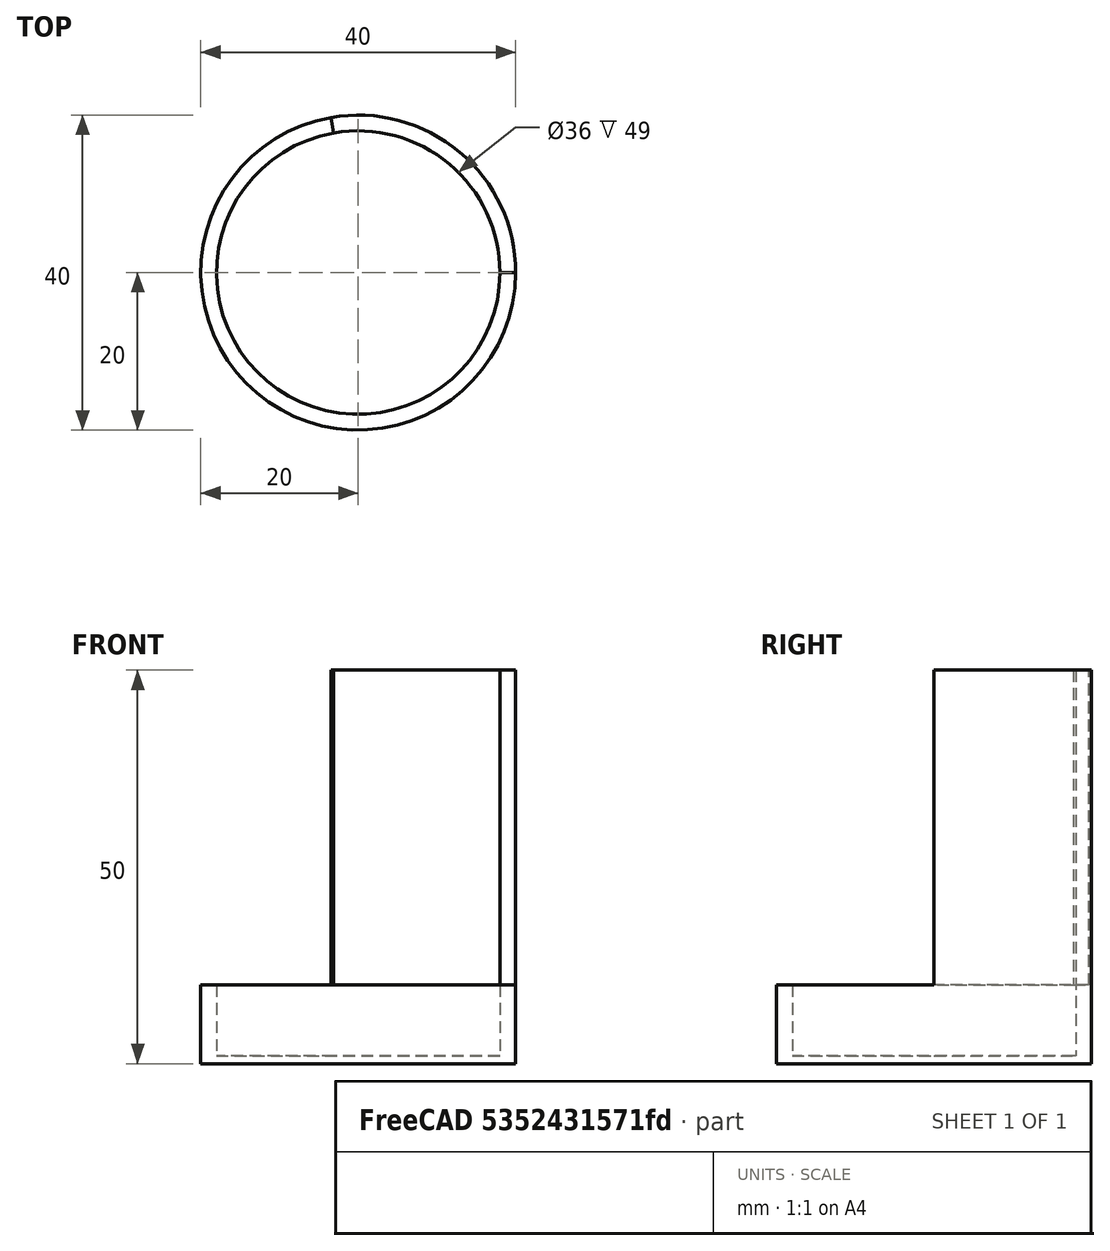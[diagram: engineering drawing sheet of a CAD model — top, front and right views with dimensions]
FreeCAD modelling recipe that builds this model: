
FCSTD DOCUMENT  (FreeCAD 0.20R29410 (Git))
Label: proyecto2
License: Creative Commons Attribution-ShareAlike
LicenseURL: http://creativecommons.org/licenses/by-sa/4.0/
objects: Part::Cylinder×4, Part::Cut×2, Part::MultiFuse×1
note: 7 computed .brp shape members not serialized (recipe doc carries the construction recipe); baked Part::Feature solids carry a one-line shape summary decoded from their .brp

FEATURE [Part::Cylinder] Cylinder
  Angle = 360
  AttacherType = Attacher::AttachEngine3D
  FirstAngle = 0
  Height = 10
  Radius = 20
  SecondAngle = 0
FEATURE [Part::Cylinder] Cylinder001
  Angle = 360
  AttacherType = Attacher::AttachEngine3D
  FirstAngle = 0
  Height = 10
  Placement = pos=(0,0,1) rot=(0,0,1;0rad)
  Radius = 18
  SecondAngle = 0
FEATURE [Part::Cut] Cut
  Base = -> Cylinder
  Refine = true
  Tool = -> Cylinder001
FEATURE [Part::Cylinder] Cylinder002
  Angle = 100
  AttacherType = Attacher::AttachEngine3D
  FirstAngle = 0
  Height = 50
  Radius = 20
  SecondAngle = 0
FEATURE [Part::Cylinder] Cylinder003
  Angle = 360
  AttacherType = Attacher::AttachEngine3D
  FirstAngle = 0
  Height = 50
  Radius = 18
  SecondAngle = 0
FEATURE [Part::Cut] Cut001
  Base = -> Cylinder002
  Refine = true
  Tool = -> Cylinder003
FEATURE [Part::MultiFuse] Fusion
  Refine = true
  Shapes = -> [Cut001,Cut]
